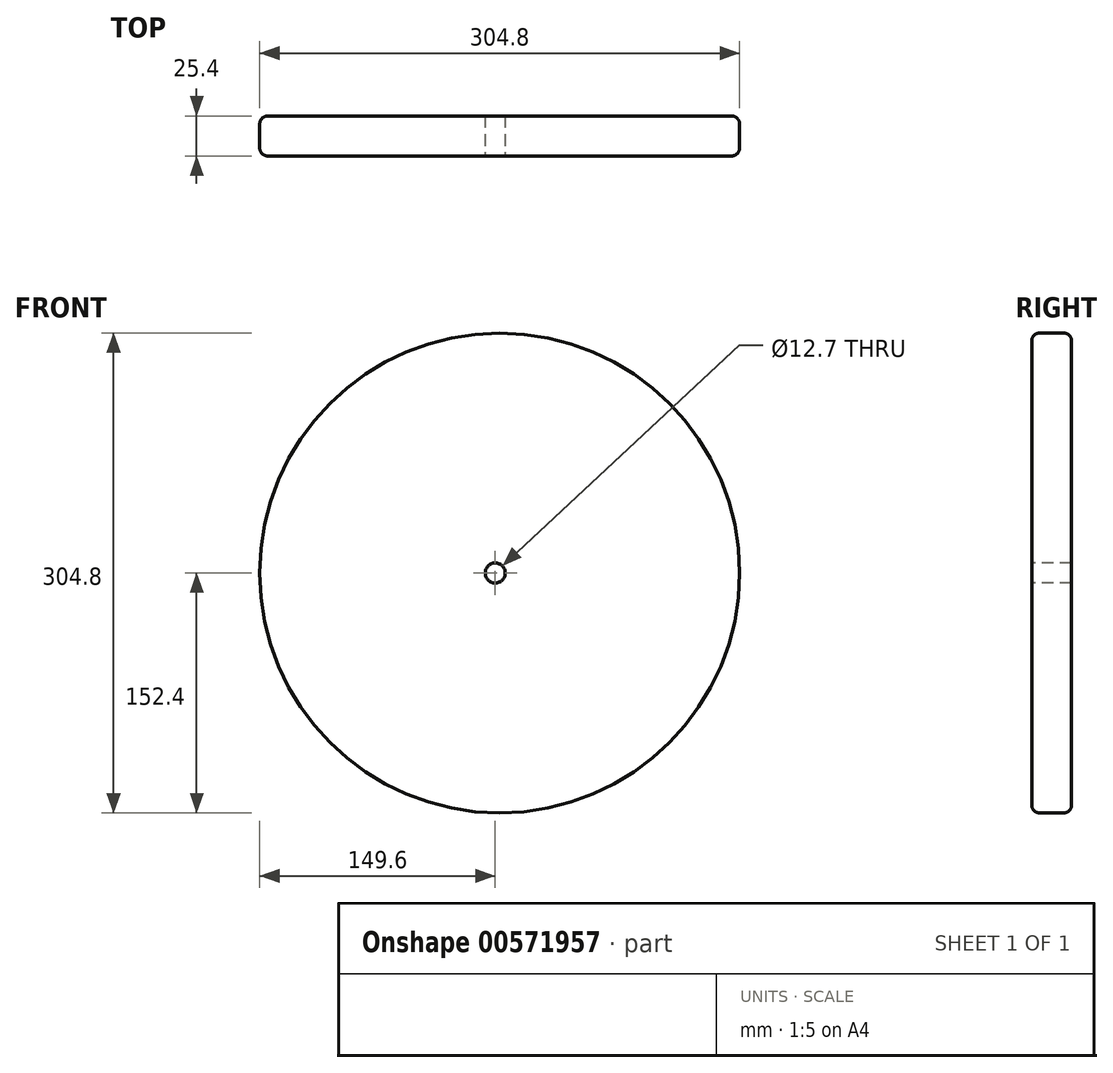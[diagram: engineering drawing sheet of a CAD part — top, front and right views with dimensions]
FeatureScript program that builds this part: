
annotation { "Feature Type Name" : "Feature", "Feature Type Description" : "" }
export const myFeature = defineFeature(function(context is Context, id is Id, definition is map)
    precondition{}
    {
        {
            var Q0;
            Q0=qCreatedBy(makeId("Front.planeOp"),FACE);
            var sketch = newSketch(context, id + "F0", { "sketchPlane" : qUnion([Q0])});
            skCircle(sketch, "E0", {"center": v(2.8, 0) * mm, "radius": 152.4 * mm});
            skSolve(sketch);
        }
        {
            var Q0;
            Q0=makeQuery(id+"F0.imprint","IMPRINT",FACE,{"disambiguationData":[TD([[makeQuery(id+"F0.imprint","IMPRINT",EDGE,{"derivedFrom":sQuery(id+"F0.wireOp",EDGE,"E0")}),1.0]])]});
            extrude(context, id + "F1", {"entities" : qUnion([Q0]), "depth" : 25.4 * mm, "offsetDistance" : 25.4 * mm});
        }
        {
            var Q0;
            Q0=makeQuery(id+"F1.opExtrude","CAP_EDGE",EDGE,{"disambiguationData":[OSD([sQuery(id+"F0.wireOp",EDGE,"E0")])],"isStart":false});
            var Q1;
            Q1=makeQuery(id+"F1.opExtrude","CAP_EDGE",EDGE,{"disambiguationData":[OSD([sQuery(id+"F0.wireOp",EDGE,"E0")])],"isStart":true});
            fillet(context, id + "F2", {"entities" : qUnion([Q0, Q1]), "radius" : 5.08 * mm, "tangentPropagation" : true, "allowEdgeOverflow" : false});
        }
        {
            var Q0;
            Q0=makeQuery(id+"F1.opExtrude","CAP_FACE",FACE,{"disambiguationData":[OSD([sQuery(id+"F0.wireOp",EDGE,"E0")])],"isStart":false});
            var sketch = newSketch(context, id + "F3", { "sketchPlane" : qUnion([Q0])});
            skCircle(sketch, "E1", {"center": v(0, 0) * mm, "radius": 6.35 * mm});
            skSolve(sketch);
        }
        {
            var Q0;
            Q0 = qSketchRegion(id + "F3", true);
            extrude(context, id + "F4", {"entities" : qUnion([Q0]), "operationType" : NewBodyOperationType.REMOVE, "oppositeDirection" : true, "depth" : 25.4 * mm, "offsetDistance" : 25.4 * mm});
        }
    });
